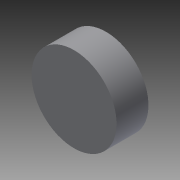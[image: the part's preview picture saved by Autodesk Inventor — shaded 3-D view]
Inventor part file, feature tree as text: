
AUTODESK INVENTOR PART (.ipt)
format: ipt  version: 2015 (Build 190159000, 159)  size: 83,456 bytes
history: native  units: mm
features: extrude x2, sketch x2
ambient origin geometry x8: Origin, YZ Plane, XZ Plane, XY Plane, X Axis, Y Axis, Z Axis, Center Point
bodies: Solid1 (feature_tree)
feature tree (4):
  extrude  "Extrusion1"  Depth=3.0mm TaperAngle=0.0deg
  extrude  "Extrusion2"  Depth=1.5mm
  sketch  "Sketch1"  dims[d0=8.0mm d1=3.0mm d2=0.0mm]
  sketch  "Sketch2"  dims[d3=3.22mm d4=1.61mm d6=1.61mm d7=1.5mm d8=0.0mm]
